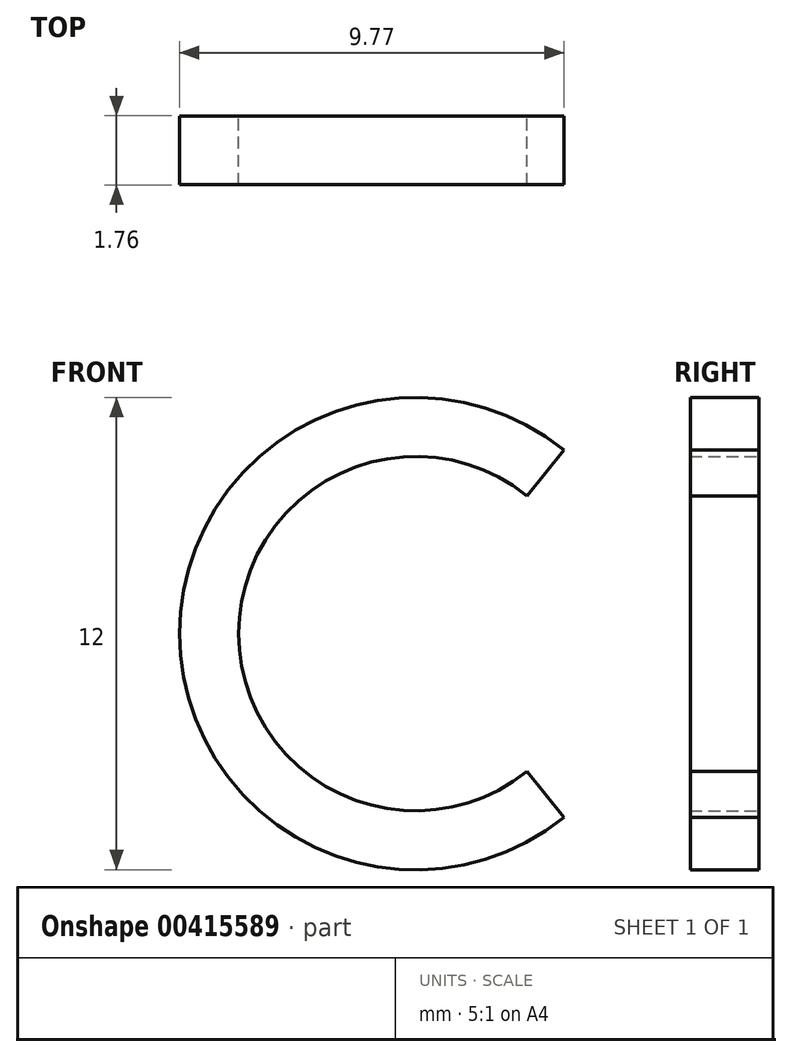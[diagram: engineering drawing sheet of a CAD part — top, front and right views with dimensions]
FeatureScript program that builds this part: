
annotation { "Feature Type Name" : "Feature", "Feature Type Description" : "" }
export const myFeature = defineFeature(function(context is Context, id is Id, definition is map)
    precondition{}
    {
        {
            var Q0;
            Q0=qCreatedBy(makeId("Front.planeOp"),FACE);
            var sketch = newSketch(context, id + "F0", { "sketchPlane" : qUnion([Q0])});
            skArc(sketch, "E0", {"start": v(2.83, 3.5) * mm, "mid": v(-4.5, 0) * mm, "end": v(2.83, -3.5) * mm});
            skArc(sketch, "E1", {"start": v(3.77, 4.67) * mm, "mid": v(-6, 0) * mm, "end": v(3.77, -4.67) * mm});
            skLineSegment(sketch, "E2", {"start": v(2.83, 3.5) * mm, "end": v(3.77, 4.67) * mm});
            skLineSegment(sketch, "E3", {"start": v(2.83, -3.5) * mm, "end": v(3.77, -4.67) * mm});
            skSolve(sketch);
        }
        {
            var Q0;
            Q0 = qSketchRegion(id + "F0", true);
            extrude(context, id + "F1", {"entities" : qUnion([Q0]), "endBound" : BoundingType.SYMMETRIC, "depth" : 1.75 * mm});
        }
    });
